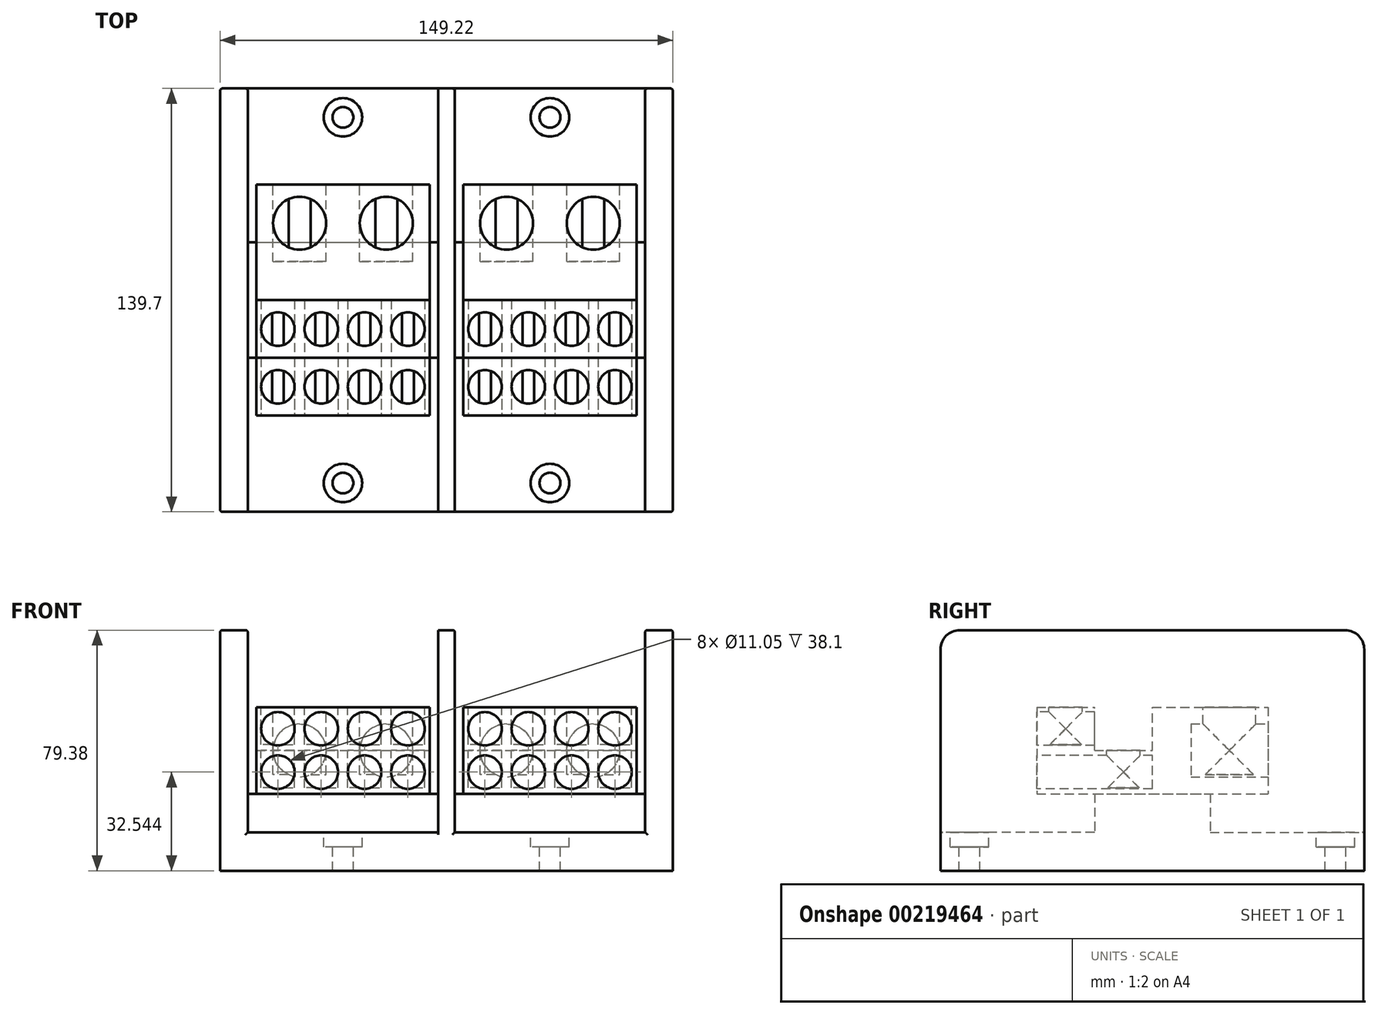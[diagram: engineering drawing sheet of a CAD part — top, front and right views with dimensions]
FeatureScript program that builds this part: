
annotation { "Feature Type Name" : "Feature", "Feature Type Description" : "" }
export const myFeature = defineFeature(function(context is Context, id is Id, definition is map)
    precondition{}
    {
        {
            var Q0;
            Q0=qCreatedBy(makeId("Top.planeOp"),FACE);
            var sketch = newSketch(context, id + "F0", { "sketchPlane" : qUnion([Q0])});
            skLineSegment(sketch, "E0.bottom", {"start": v(-74.61, -69.85) * mm, "end": v(74.61, -69.85) * mm});
            skLineSegment(sketch, "E0.top", {"start": v(-74.61, 69.85) * mm, "end": v(74.61, 69.85) * mm});
            skLineSegment(sketch, "E0.left", {"start": v(-74.61, -69.85) * mm, "end": v(-74.61, 69.85) * mm});
            skLineSegment(sketch, "E0.right", {"start": v(74.61, -69.85) * mm, "end": v(74.61, 69.85) * mm});
            skPoint(sketch, "E0.middle", {"position": v(0, 0) * mm});
            skSolve(sketch);
        }
        {
            var Q0;
            Q0=qSketchRegion(id+"F0",true);
            extrude(context, id + "F1", {"entities" : qUnion([Q0]), "depth" : 12.7 * mm});
        }
        {
            var Q0;
            Q0=makeQuery(id+"F1.opExtrude","CAP_FACE",FACE,{"disambiguationData":[OSD([sQuery(id+"F0.wireOp",EDGE,"E0.bottom"),sQuery(id+"F0.wireOp",EDGE,"E0.top"),sQuery(id+"F0.wireOp",EDGE,"E0.left"),sQuery(id+"F0.wireOp",EDGE,"E0.right")])],"isStart":false});
            var sketch = newSketch(context, id + "F2", { "sketchPlane" : qUnion([Q0])});
            skCircle(sketch, "E1", {"center": v(-34.13, 60.33) * mm, "radius": 3.43 * mm});
            skCircle(sketch, "E2", {"center": v(34.13, 60.33) * mm, "radius": 3.43 * mm});
            skCircle(sketch, "E3", {"center": v(-34.13, -60.33) * mm, "radius": 3.43 * mm});
            skCircle(sketch, "E4", {"center": v(34.13, -60.32) * mm, "radius": 3.43 * mm});
            skSolve(sketch);
        }
        {
            var Q0;
            Q0=qSketchRegion(id+"F2",true);
            extrude(context, id + "F3", {"entities" : qUnion([Q0]), "operationType" : NewBodyOperationType.REMOVE, "oppositeDirection" : true, "depth" : 12.7 * mm});
        }
        {
            var Q0;
            Q0=makeQuery(id+"F1.opExtrude","CAP_FACE",FACE,{"disambiguationData":[OSD([sQuery(id+"F0.wireOp",EDGE,"E0.bottom"),sQuery(id+"F0.wireOp",EDGE,"E0.top"),sQuery(id+"F0.wireOp",EDGE,"E0.left"),sQuery(id+"F0.wireOp",EDGE,"E0.right")])],"isStart":false});
            var sketch = newSketch(context, id + "F4", { "sketchPlane" : qUnion([Q0])});
            skCircle(sketch, "E5", {"center": v(-34.13, 60.33) * mm, "radius": 6.35 * mm});
            skCircle(sketch, "E6", {"center": v(34.13, 60.33) * mm, "radius": 6.35 * mm});
            skCircle(sketch, "E7", {"center": v(-34.13, -60.33) * mm, "radius": 6.35 * mm});
            skCircle(sketch, "E8", {"center": v(34.13, -60.32) * mm, "radius": 6.35 * mm});
            skSolve(sketch);
        }
        {
            var Q0;
            Q0=qSketchRegion(id+"F4",true);
            extrude(context, id + "F5", {"entities" : qUnion([Q0]), "operationType" : NewBodyOperationType.REMOVE, "oppositeDirection" : true, "depth" : 4.83 * mm});
        }
        {
            var Q0;
            Q0=makeQuery(id+"F1.opExtrude","CAP_FACE",FACE,{"disambiguationData":[OSD([sQuery(id+"F0.wireOp",EDGE,"E0.bottom"),sQuery(id+"F0.wireOp",EDGE,"E0.top"),sQuery(id+"F0.wireOp",EDGE,"E0.left"),sQuery(id+"F0.wireOp",EDGE,"E0.right")])],"isStart":false});
            var sketch = newSketch(context, id + "F6", { "sketchPlane" : qUnion([Q0])});
            skLineSegment(sketch, "E9.bottom", {"start": v(-65.48, -19.05) * mm, "end": v(-2.78, -19.05) * mm});
            skLineSegment(sketch, "E9.top", {"start": v(-65.48, 19.05) * mm, "end": v(-2.78, 19.05) * mm});
            skLineSegment(sketch, "E9.left", {"start": v(-65.48, -19.05) * mm, "end": v(-65.48, 19.05) * mm});
            skLineSegment(sketch, "E9.right", {"start": v(-2.78, -19.05) * mm, "end": v(-2.78, 19.05) * mm});
            skPoint(sketch, "E9.middle", {"position": v(-34.13, 0) * mm});
            skLineSegment(sketch, "E10.bottom", {"start": v(2.78, -19.05) * mm, "end": v(65.48, -19.05) * mm});
            skLineSegment(sketch, "E10.top", {"start": v(2.78, 19.05) * mm, "end": v(65.48, 19.05) * mm});
            skLineSegment(sketch, "E10.left", {"start": v(2.78, -19.05) * mm, "end": v(2.78, 19.05) * mm});
            skLineSegment(sketch, "E10.right", {"start": v(65.48, -19.05) * mm, "end": v(65.48, 19.05) * mm});
            skPoint(sketch, "E10.middle", {"position": v(34.13, 0) * mm});
            skPoint(sketch, "E10.middle.positionSnap0", {"position": v(-2.78, 0) * mm});
            skPoint(sketch, "E10.centerSnap0", {"position": v(-2.78, 0) * mm});
            skSolve(sketch);
        }
        {
            var Q0;
            Q0=qSketchRegion(id+"F6",true);
            extrude(context, id + "F7", {"entities" : qUnion([Q0]), "operationType" : NewBodyOperationType.ADD, "depth" : 12.7 * mm});
        }
        {
            var Q0;
            Q0=makeQuery(id+"F1.opExtrude","CAP_FACE",FACE,{"disambiguationData":[OSD([sQuery(id+"F0.wireOp",EDGE,"E0.bottom"),sQuery(id+"F0.wireOp",EDGE,"E0.top"),sQuery(id+"F0.wireOp",EDGE,"E0.left"),sQuery(id+"F0.wireOp",EDGE,"E0.right")])],"isStart":false});
            var sketch = newSketch(context, id + "F8", { "sketchPlane" : qUnion([Q0])});
            skLineSegment(sketch, "E11.bottom", {"start": v(-74.61, 69.85) * mm, "end": v(-65.48, 69.85) * mm});
            skLineSegment(sketch, "E11.top", {"start": v(-74.61, -69.85) * mm, "end": v(-65.48, -69.85) * mm});
            skLineSegment(sketch, "E11.left", {"start": v(-74.61, 69.85) * mm, "end": v(-74.61, -69.85) * mm});
            skLineSegment(sketch, "E11.right", {"start": v(-65.48, 69.85) * mm, "end": v(-65.48, -69.85) * mm});
            skLineSegment(sketch, "E12.bottom", {"start": v(-2.78, 69.85) * mm, "end": v(2.78, 69.85) * mm});
            skLineSegment(sketch, "E12.top", {"start": v(-2.78, -69.85) * mm, "end": v(2.78, -69.85) * mm});
            skLineSegment(sketch, "E12.left", {"start": v(-2.78, 69.85) * mm, "end": v(-2.78, -69.85) * mm});
            skLineSegment(sketch, "E12.right", {"start": v(2.78, 69.85) * mm, "end": v(2.78, -69.85) * mm});
            skLineSegment(sketch, "E13.bottom", {"start": v(65.48, 69.85) * mm, "end": v(74.61, 69.85) * mm});
            skLineSegment(sketch, "E13.top", {"start": v(65.48, -69.85) * mm, "end": v(74.61, -69.85) * mm});
            skLineSegment(sketch, "E13.left", {"start": v(65.48, 69.85) * mm, "end": v(65.48, -69.85) * mm});
            skLineSegment(sketch, "E13.right", {"start": v(74.61, 69.85) * mm, "end": v(74.61, -69.85) * mm});
            skSolve(sketch);
        }
        {
            var Q0;
            Q0=qSketchRegion(id+"F8",true);
            extrude(context, id + "F9", {"entities" : qUnion([Q0]), "operationType" : NewBodyOperationType.ADD, "depth" : 66.67 * mm});
        }
        {
            var Q0;
            Q0=makeQuery(id+"F7.opExtrude","CAP_FACE",FACE,{"disambiguationData":[OSD([sQuery(id+"F6.wireOp",EDGE,"E9.bottom"),sQuery(id+"F6.wireOp",EDGE,"E9.top"),sQuery(id+"F6.wireOp",EDGE,"E9.left"),sQuery(id+"F6.wireOp",EDGE,"E9.right")])],"isStart":false});
            var sketch = newSketch(context, id + "F10", { "sketchPlane" : qUnion([Q0])});
            skLineSegment(sketch, "E14.bottom", {"start": v(-5.56, -38.1) * mm, "end": v(-62.7, -38.1) * mm});
            skLineSegment(sketch, "E14.top", {"start": v(-5.56, 38.1) * mm, "end": v(-62.7, 38.1) * mm});
            skLineSegment(sketch, "E14.left", {"start": v(-5.56, -38.1) * mm, "end": v(-5.56, 38.1) * mm});
            skLineSegment(sketch, "E14.right", {"start": v(-62.7, -38.1) * mm, "end": v(-62.7, 38.1) * mm});
            skPoint(sketch, "E14.middle", {"position": v(-34.13, 0) * mm});
            skSolve(sketch);
        }
        {
            var Q0;
            Q0=qSketchRegion(id+"F10",true);
            extrude(context, id + "F11", {"entities" : qUnion([Q0]), "depth" : 28.57 * mm});
        }
        {
            var Q0;
            Q0=makeQuery(id+"F11.opExtrude","SWEPT_FACE",FACE,{"disambiguationData":[OSD([sQuery(id+"F10.wireOp",EDGE,"E14.bottom")])]});
            var sketch = newSketch(context, id + "F12", { "sketchPlane" : qUnion([Q0])});
            skCircle(sketch, "E15", {"center": v(-55.56, 46.83) * mm, "radius": 5.52 * mm});
            skCircle(sketch, "E16", {"center": v(-41.27, 46.83) * mm, "radius": 5.52 * mm});
            skCircle(sketch, "E17", {"center": v(-26.99, 46.83) * mm, "radius": 5.52 * mm});
            skCircle(sketch, "E18", {"center": v(-12.7, 46.83) * mm, "radius": 5.52 * mm});
            skCircle(sketch, "E19", {"center": v(-55.56, 32.54) * mm, "radius": 5.52 * mm});
            skCircle(sketch, "E20", {"center": v(-41.27, 32.54) * mm, "radius": 5.52 * mm});
            skCircle(sketch, "E21", {"center": v(-26.99, 32.54) * mm, "radius": 5.52 * mm});
            skCircle(sketch, "E22", {"center": v(-12.7, 32.54) * mm, "radius": 5.52 * mm});
            skSolve(sketch);
        }
        {
            var Q0;
            Q0=makeQuery(id+"F11.opExtrude","CAP_FACE",FACE,{"disambiguationData":[OSD([sQuery(id+"F10.wireOp",EDGE,"E14.bottom"),sQuery(id+"F10.wireOp",EDGE,"E14.top"),sQuery(id+"F10.wireOp",EDGE,"E14.left"),sQuery(id+"F10.wireOp",EDGE,"E14.right")])],"isStart":false});
            var sketch = newSketch(context, id + "F13", { "sketchPlane" : qUnion([Q0])});
            skLineSegment(sketch, "E23.bottom", {"start": v(-62.7, 0) * mm, "end": v(-5.56, 0) * mm});
            skLineSegment(sketch, "E23.top", {"start": v(-62.7, -19.05) * mm, "end": v(-5.56, -19.05) * mm});
            skLineSegment(sketch, "E23.left", {"start": v(-62.7, 0) * mm, "end": v(-62.7, -19.05) * mm});
            skLineSegment(sketch, "E23.right", {"start": v(-5.56, 0) * mm, "end": v(-5.56, -19.05) * mm});
            skSolve(sketch);
        }
        {
            var Q0;
            Q0=qSketchRegion(id+"F13",true);
            extrude(context, id + "F14", {"entities" : qUnion([Q0]), "operationType" : NewBodyOperationType.REMOVE, "oppositeDirection" : true, "depth" : 14.29 * mm});
        }
        {
            var Q0;
            Q0=qSketchRegion(id+"F12",true);
            extrude(context, id + "F15", {"entities" : qUnion([Q0]), "operationType" : NewBodyOperationType.REMOVE, "oppositeDirection" : true, "depth" : 19.05 * mm});
        }
        {
            var Q0;
            Q0=makeQuery(id+"F15.boolean.opBoolean","COPY",FACE,{"derivedFrom":makeQuery(id+"F15.opExtrude","CAP_FACE",FACE,{"disambiguationData":[OSD([sQuery(id+"F12.wireOp",EDGE,"E19")])],"isStart":false})});
            var Q1;
            Q1=makeQuery(id+"F15.boolean.opBoolean","COPY",FACE,{"derivedFrom":makeQuery(id+"F15.opExtrude","CAP_FACE",FACE,{"disambiguationData":[OSD([sQuery(id+"F12.wireOp",EDGE,"E20")])],"isStart":false})});
            var Q2;
            Q2=makeQuery(id+"F15.boolean.opBoolean","COPY",FACE,{"derivedFrom":makeQuery(id+"F15.opExtrude","CAP_FACE",FACE,{"disambiguationData":[OSD([sQuery(id+"F12.wireOp",EDGE,"E21")])],"isStart":false})});
            var Q3;
            Q3=makeQuery(id+"F15.boolean.opBoolean","COPY",FACE,{"derivedFrom":makeQuery(id+"F15.opExtrude","CAP_FACE",FACE,{"disambiguationData":[OSD([sQuery(id+"F12.wireOp",EDGE,"E22")])],"isStart":false})});
            extrude(context, id + "F16", {"entities" : qUnion([Q0, Q1, Q2, Q3]), "operationType" : NewBodyOperationType.REMOVE, "oppositeDirection" : true, "depth" : 19.05 * mm});
        }
        {
            var Q0;
            {var subQ0=sQuery(id+"F10.wireOp",EDGE,"E14.bottom");var subQ1=sQuery(id+"F10.wireOp",EDGE,"E14.left");var subQ2=sQuery(id+"F10.wireOp",EDGE,"E14.right");Q0=makeQuery(id+"F14.boolean.opBoolean","SPLIT",FACE,{"disambiguationData":[TD([makeQuery(id+"F11.opExtrude","SWEPT_FACE",FACE,{"disambiguationData":[OSD([subQ0])]})])],"derivedFrom":makeQuery(id+"F11.opExtrude","CAP_FACE",FACE,{"disambiguationData":[OSD([subQ0,sQuery(id+"F10.wireOp",EDGE,"E14.top"),subQ1,subQ2])],"isStart":false})});}
            var sketch = newSketch(context, id + "F17", { "sketchPlane" : qUnion([Q0])});
            skCircle(sketch, "E24", {"center": v(-55.56, -28.58) * mm, "radius": 5.52 * mm});
            skPoint(sketch, "E24.centerSnap0", {"position": v(-62.7, -28.58) * mm});
            skCircle(sketch, "E25", {"center": v(-41.27, -28.57) * mm, "radius": 5.52 * mm});
            skCircle(sketch, "E26", {"center": v(-26.99, -28.57) * mm, "radius": 5.52 * mm});
            skCircle(sketch, "E27", {"center": v(-12.7, -28.57) * mm, "radius": 5.52 * mm});
            skSolve(sketch);
        }
        {
            var Q0;
            Q0=qSketchRegion(id+"F17",true);
            extrude(context, id + "F18", {"entities" : qUnion([Q0]), "operationType" : NewBodyOperationType.REMOVE, "oppositeDirection" : true, "depth" : 12.32 * mm});
        }
        {
            var Q0;
            Q0=makeQuery(id+"F14.boolean.opBoolean","COPY",FACE,{"derivedFrom":makeQuery(id+"F14.opExtrude","CAP_FACE",FACE,{"disambiguationData":[OSD([sQuery(id+"F13.wireOp",EDGE,"E23.bottom"),sQuery(id+"F13.wireOp",EDGE,"E23.top"),sQuery(id+"F13.wireOp",EDGE,"E23.left"),sQuery(id+"F13.wireOp",EDGE,"E23.right")])],"isStart":false})});
            var sketch = newSketch(context, id + "F19", { "sketchPlane" : qUnion([Q0])});
            skCircle(sketch, "E28", {"center": v(-55.56, -9.52) * mm, "radius": 5.52 * mm});
            skPoint(sketch, "E28.centerSnap0", {"position": v(-62.7, -9.52) * mm});
            skCircle(sketch, "E29", {"center": v(-41.27, -9.52) * mm, "radius": 5.52 * mm});
            skCircle(sketch, "E30", {"center": v(-26.99, -9.52) * mm, "radius": 5.52 * mm});
            skCircle(sketch, "E31", {"center": v(-12.7, -9.52) * mm, "radius": 5.52 * mm});
            skSolve(sketch);
        }
        {
            var Q0;
            Q0=qSketchRegion(id+"F19",true);
            extrude(context, id + "F20", {"entities" : qUnion([Q0]), "operationType" : NewBodyOperationType.REMOVE, "oppositeDirection" : true, "depth" : 12.32 * mm});
        }
        {
            var Q0;
            {var subQ0=sQuery(id+"F10.wireOp",EDGE,"E14.top");var subQ1=sQuery(id+"F10.wireOp",EDGE,"E14.right");var subQ2=sQuery(id+"F10.wireOp",EDGE,"E14.left");Q0=makeQuery(id+"F14.boolean.opBoolean","SPLIT",FACE,{"disambiguationData":[TD([makeQuery(id+"F11.opExtrude","SWEPT_FACE",FACE,{"disambiguationData":[OSD([subQ0])]})])],"derivedFrom":makeQuery(id+"F11.opExtrude","CAP_FACE",FACE,{"disambiguationData":[OSD([sQuery(id+"F10.wireOp",EDGE,"E14.bottom"),subQ0,subQ2,subQ1])],"isStart":false})});}
            var sketch = newSketch(context, id + "F21", { "sketchPlane" : qUnion([Q0])});
            skCircle(sketch, "E32", {"center": v(-19.84, 25.4) * mm, "radius": 8.73 * mm});
            skCircle(sketch, "E33", {"center": v(-48.42, 25.4) * mm, "radius": 8.73 * mm});
            skSolve(sketch);
        }
        {
            var Q0;
            Q0=makeQuery(id+"F11.opExtrude","SWEPT_FACE",FACE,{"disambiguationData":[OSD([sQuery(id+"F10.wireOp",EDGE,"E14.top")])]});
            var sketch = newSketch(context, id + "F22", { "sketchPlane" : qUnion([Q0])});
            skCircle(sketch, "E34", {"center": v(19.84, 39.69) * mm, "radius": 8.73 * mm});
            skPoint(sketch, "E34.centerSnap0", {"position": v(5.56, 39.69) * mm});
            skCircle(sketch, "E35", {"center": v(48.42, 39.69) * mm, "radius": 8.73 * mm});
            skSolve(sketch);
        }
        {
            var Q0;
            Q0=qSketchRegion(id+"F22",true);
            extrude(context, id + "F23", {"entities" : qUnion([Q0]), "operationType" : NewBodyOperationType.REMOVE, "oppositeDirection" : true, "depth" : 25.4 * mm});
        }
        {
            var Q0;
            Q0=qSketchRegion(id+"F21",true);
            extrude(context, id + "F24", {"entities" : qUnion([Q0]), "operationType" : NewBodyOperationType.REMOVE, "oppositeDirection" : true, "depth" : 22.22 * mm});
        }
        {
            var Q0;
            Q0=makeQuery(id+"F11.opExtrude","SWEPT_BODY",BODY,{"disambiguationData":[OSD([sQuery(id+"F10.wireOp",EDGE,"E14.bottom"),sQuery(id+"F10.wireOp",EDGE,"E14.top"),sQuery(id+"F10.wireOp",EDGE,"E14.left"),sQuery(id+"F10.wireOp",EDGE,"E14.right")])]});
            transform(context, id + "F25", {"entities" : qUnion([Q0]), "transformType" : TransformType.TRANSLATION_3D, "dx" : 68.26 * mm, "dy" : 0 * mm, "dz" : 0 * mm, "makeCopy" : true});
        }
        {
            var Q0;
            Q0=makeQuery(id+"F9.opExtrude","CAP_EDGE",EDGE,{"disambiguationData":[OSD([sQuery(id+"F8.wireOp",EDGE,"E11.top")])],"isStart":false});
            var Q1;
            Q1=makeQuery(id+"F9.opExtrude","CAP_EDGE",EDGE,{"disambiguationData":[OSD([sQuery(id+"F8.wireOp",EDGE,"E12.top")])],"isStart":false});
            var Q2;
            Q2=makeQuery(id+"F9.opExtrude","CAP_EDGE",EDGE,{"disambiguationData":[OSD([sQuery(id+"F8.wireOp",EDGE,"E13.top")])],"isStart":false});
            var Q3;
            Q3=makeQuery(id+"F9.opExtrude","CAP_EDGE",EDGE,{"disambiguationData":[OSD([sQuery(id+"F8.wireOp",EDGE,"E13.bottom")])],"isStart":false});
            var Q4;
            Q4=makeQuery(id+"F9.opExtrude","CAP_EDGE",EDGE,{"disambiguationData":[OSD([sQuery(id+"F8.wireOp",EDGE,"E12.bottom")])],"isStart":false});
            var Q5;
            Q5=makeQuery(id+"F9.opExtrude","CAP_EDGE",EDGE,{"disambiguationData":[OSD([sQuery(id+"F8.wireOp",EDGE,"E11.bottom")])],"isStart":false});
            fillet(context, id + "F26", {"entities" : qUnion([Q0, Q1, Q2, Q3, Q4, Q5]), "radius" : 6.35 * mm, "tangentPropagation" : true});
        }
        {
            var Q0;
            Q0=makeQuery(id+"F9.boolean.opBoolean","MERGE",EDGE,{"derivedFrom":[makeQuery(id+"F1.opExtrude","SWEPT_EDGE",EDGE,{"disambiguationData":[OSD([sQuery(id+"F0.wireOp",EDGE,"E0.bottom"),sQuery(id+"F0.wireOp",EDGE,"E0.right")])]}),makeQuery(id+"F9.opExtrude","SWEPT_EDGE",EDGE,{"disambiguationData":[OSD([sQuery(id+"F8.wireOp",EDGE,"E13.top"),sQuery(id+"F8.wireOp",EDGE,"E13.right")])]})]});
            var Q1;
            {var subQ0=sQuery(id+"F0.wireOp",EDGE,"E0.bottom");Q1=makeQuery(id+"F9.boolean.opBoolean","SPLIT",EDGE,{"disambiguationData":[TD([makeQuery(id+"F9.opExtrude","SWEPT_FACE",FACE,{"disambiguationData":[OSD([sQuery(id+"F8.wireOp",EDGE,"E12.right")])]})])],"derivedFrom":makeQuery(id+"F1.opExtrude","CAP_EDGE",EDGE,{"disambiguationData":[OSD([subQ0])],"isStart":false})});}
            var Q2;
            Q2=makeQuery(id+"F9.opExtrude","SWEPT_EDGE",EDGE,{"disambiguationData":[OSD([sQuery(id+"F0.wireOp",EDGE,"E0.bottom"),sQuery(id+"F8.wireOp",EDGE,"E13.top"),sQuery(id+"F8.wireOp",EDGE,"E13.left")])]});
            var Q3;
            Q3=makeQuery(id+"F9.opExtrude","SWEPT_EDGE",EDGE,{"disambiguationData":[OSD([sQuery(id+"F0.wireOp",EDGE,"E0.bottom"),sQuery(id+"F8.wireOp",EDGE,"E12.top"),sQuery(id+"F8.wireOp",EDGE,"E12.right")])]});
            var Q4;
            {var subQ0=sQuery(id+"F0.wireOp",EDGE,"E0.bottom");Q4=makeQuery(id+"F9.boolean.opBoolean","SPLIT",EDGE,{"disambiguationData":[TD([makeQuery(id+"F9.opExtrude","SWEPT_FACE",FACE,{"disambiguationData":[OSD([sQuery(id+"F8.wireOp",EDGE,"E11.right")])]})])],"derivedFrom":makeQuery(id+"F1.opExtrude","CAP_EDGE",EDGE,{"disambiguationData":[OSD([subQ0])],"isStart":false})});}
            var Q5;
            Q5=makeQuery(id+"F9.opExtrude","SWEPT_EDGE",EDGE,{"disambiguationData":[OSD([sQuery(id+"F0.wireOp",EDGE,"E0.bottom"),sQuery(id+"F8.wireOp",EDGE,"E11.top"),sQuery(id+"F8.wireOp",EDGE,"E11.right")])]});
            var Q6;
            Q6=makeQuery(id+"F9.boolean.opBoolean","MERGE",EDGE,{"derivedFrom":[makeQuery(id+"F1.opExtrude","SWEPT_EDGE",EDGE,{"disambiguationData":[OSD([sQuery(id+"F0.wireOp",EDGE,"E0.bottom"),sQuery(id+"F0.wireOp",EDGE,"E0.left")])]}),makeQuery(id+"F9.opExtrude","SWEPT_EDGE",EDGE,{"disambiguationData":[OSD([sQuery(id+"F8.wireOp",EDGE,"E11.top"),sQuery(id+"F8.wireOp",EDGE,"E11.left")])]})]});
            var Q7;
            {var subQ0=sQuery(id+"F0.wireOp",EDGE,"E0.top");Q7=makeQuery(id+"F9.boolean.opBoolean","SPLIT",EDGE,{"disambiguationData":[TD([makeQuery(id+"F9.opExtrude","SWEPT_FACE",FACE,{"disambiguationData":[OSD([sQuery(id+"F8.wireOp",EDGE,"E12.right")])]})])],"derivedFrom":makeQuery(id+"F1.opExtrude","CAP_EDGE",EDGE,{"disambiguationData":[OSD([subQ0])],"isStart":false})});}
            var Q8;
            {var subQ0=sQuery(id+"F0.wireOp",EDGE,"E0.top");Q8=makeQuery(id+"F9.boolean.opBoolean","SPLIT",EDGE,{"disambiguationData":[TD([makeQuery(id+"F9.opExtrude","SWEPT_FACE",FACE,{"disambiguationData":[OSD([sQuery(id+"F8.wireOp",EDGE,"E11.right")])]})])],"derivedFrom":makeQuery(id+"F1.opExtrude","CAP_EDGE",EDGE,{"disambiguationData":[OSD([subQ0])],"isStart":false})});}
            fillet(context, id + "F27", {"entities" : qUnion([Q0, Q1, Q2, Q3, Q4, Q5, Q6, Q7, Q8]), "radius" : 0.76 * mm, "tangentPropagation" : true});
        }
    });
